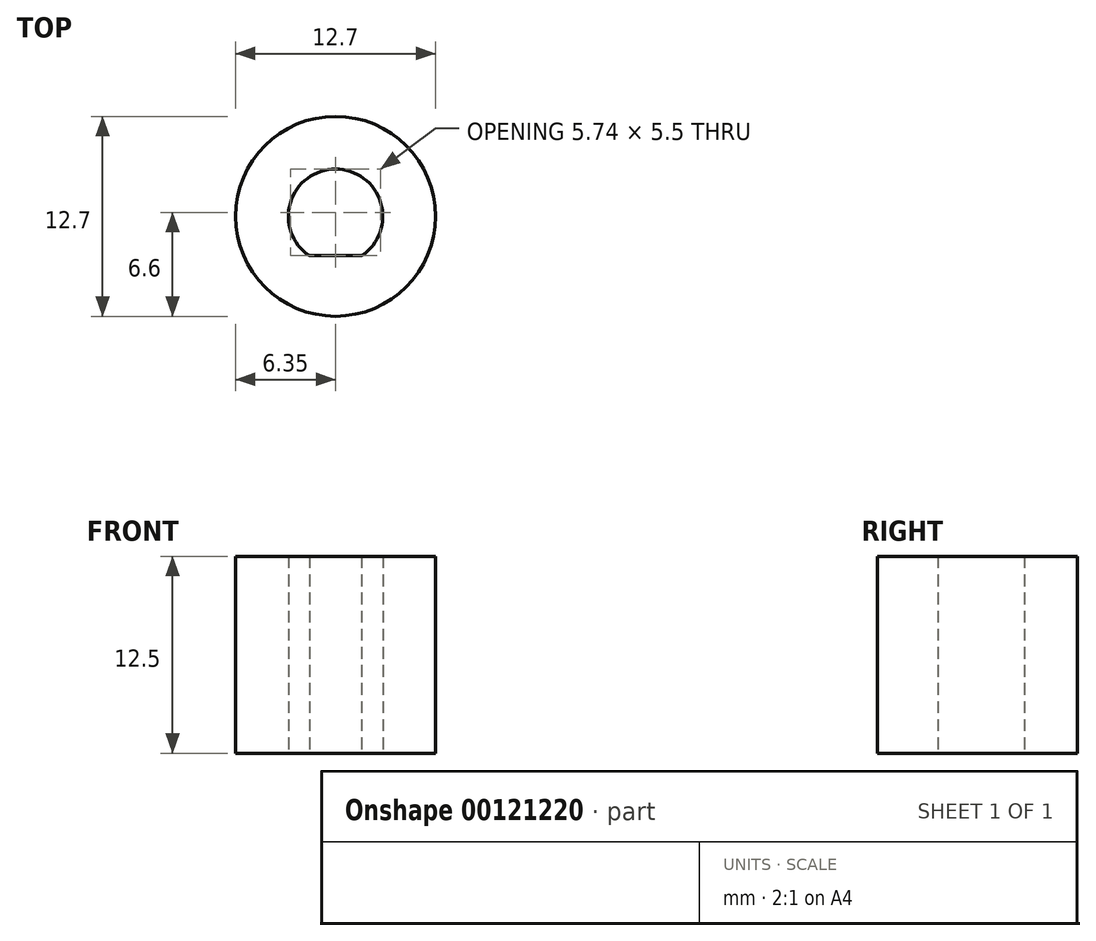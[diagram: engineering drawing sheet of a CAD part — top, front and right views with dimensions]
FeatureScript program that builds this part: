
annotation { "Feature Type Name" : "Feature", "Feature Type Description" : "" }
export const myFeature = defineFeature(function(context is Context, id is Id, definition is map)
    precondition{}
    {
        {
            var Q0;
            Q0=qCreatedBy(makeId("Top.planeOp"),FACE);
            var sketch = newSketch(context, id + "F0", { "sketchPlane" : qUnion([Q0])});
            skArc(sketch, "E0", {"start": v(1.66, -2.5) * mm, "mid": v(0, 3) * mm, "end": v(-1.66, -2.5) * mm});
            skLineSegment(sketch, "E1", {"start": v(-1.66, -2.5) * mm, "end": v(1.66, -2.5) * mm});
            skCircle(sketch, "E2", {"center": v(0, 0) * mm, "radius": 6.35 * mm});
            skSolve(sketch);
        }
        {
            var Q0;
            Q0=makeQuery(id+"F0.imprint","IMPRINT",FACE,{"disambiguationData":[TD([[makeQuery(id+"F0.imprint","IMPRINT",EDGE,{"derivedFrom":sQuery(id+"F0.wireOp",EDGE,"E0")}),-1.0]])]});
            extrude(context, id + "F1", {"entities" : qUnion([Q0]), "depth" : 12.5 * mm});
        }
    });
